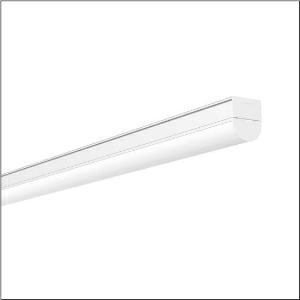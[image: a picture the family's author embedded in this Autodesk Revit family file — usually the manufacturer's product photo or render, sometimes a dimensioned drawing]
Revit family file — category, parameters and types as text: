
# Revit family: ecopack_31_51lj12dkm40a
name_source: partatom
category: Lighting Fixtures
units: mm (PartAtom-declared; Revit-internal decimal feet)

## family parameters
Cut with Voids When Loaded = No
Host = Face
Light Source = No
Part Type = Normal
Room Calculation Point = No
Round Connector Dimension = Use Diameter
Shared = No

## types (1)
- --- (1 x LED, 4290 lm, 33 W, 5000K)
    Apparent Load = 33 VA
    CIE Flux Codes = 39 67 87 89 100
    Color Rendering = 80
    Color Temperature = 5000K
    Default Elevation = 1800 mm
    Description = Ecopack 31, diffuser luminaire, primary optical cover: cover, of PC, frosted, light emission: direct distribution, primary light characteristic: symmetric, installation type: surface-mounted, LED, rated luminous flux: 4.300lm, luminous efficacy: 130lm/W, light colour: 830/840/850, colour temperature: 3000/4000/5000K, control gear: DALI 2, with terminal, 5-pole, mains connection: 220..240V, AC, 50/60Hz, rated input power: 33W, housing, of aluminium, traffic white (RAL 9016), length: 1.150mm, width: 56mm, height: 68mm, end cap, of PC, white, protection rating (complete): IP20, insulation class (complete): insulation class I (protective earthing), certification: CE, impact resistance: IK06, permissible operating ambient temperature: -20..+40°C, packaging unit: 1 piece
    Height = 68 mm
    Lamp = 1 x LED
    Lamp Light Flux = 4290 lm
    Lamp Power = 33 W
    Lamp count = 1
    Length = 1149 mm
    Luminous efficacy = 130 lm/W
    Manufacturer = Siteco
    ModVariant = No
    Model = 51LJ12DKM40A
    Mounting Place = Ceiling
    Mounting Type = Surface mounted
    Number of Poles = 1
    OnlyDefault = Yes
    Power Factor = 1
    Product Name = Ecopack 31
    Product group = diffuser luminaire
    ProductGroupID = 307
    Protection Class = Protection class I
    Protection Degree = IP 20
    RLX_Detail_Level = 1
    RLX_Emergency_Light_Flux = 0 lm
    RLX_Emergency_Type = 0
    RLX_Emergency_Type_DB = No
    RlxData = <blob elided: 24889 chars, md5=76d16ef6>
    Socket = socket
    Standby Power = 0 W
    System Light Flux = 4290 lm
    System Power = 33 W
    Type Comments = individual setting: colour temperature 5000K
    Type Image = l_1007030.jpg
    URL = http://relux.com
    VarID = @adj_175041
    Voltage = 0 V
    Weight = 0.00 kg
    Width = 56 mm

## geometry (parser evidence)
native form markers: Blend x4, Sweep x12
no freeform markers — native parametric forms only
